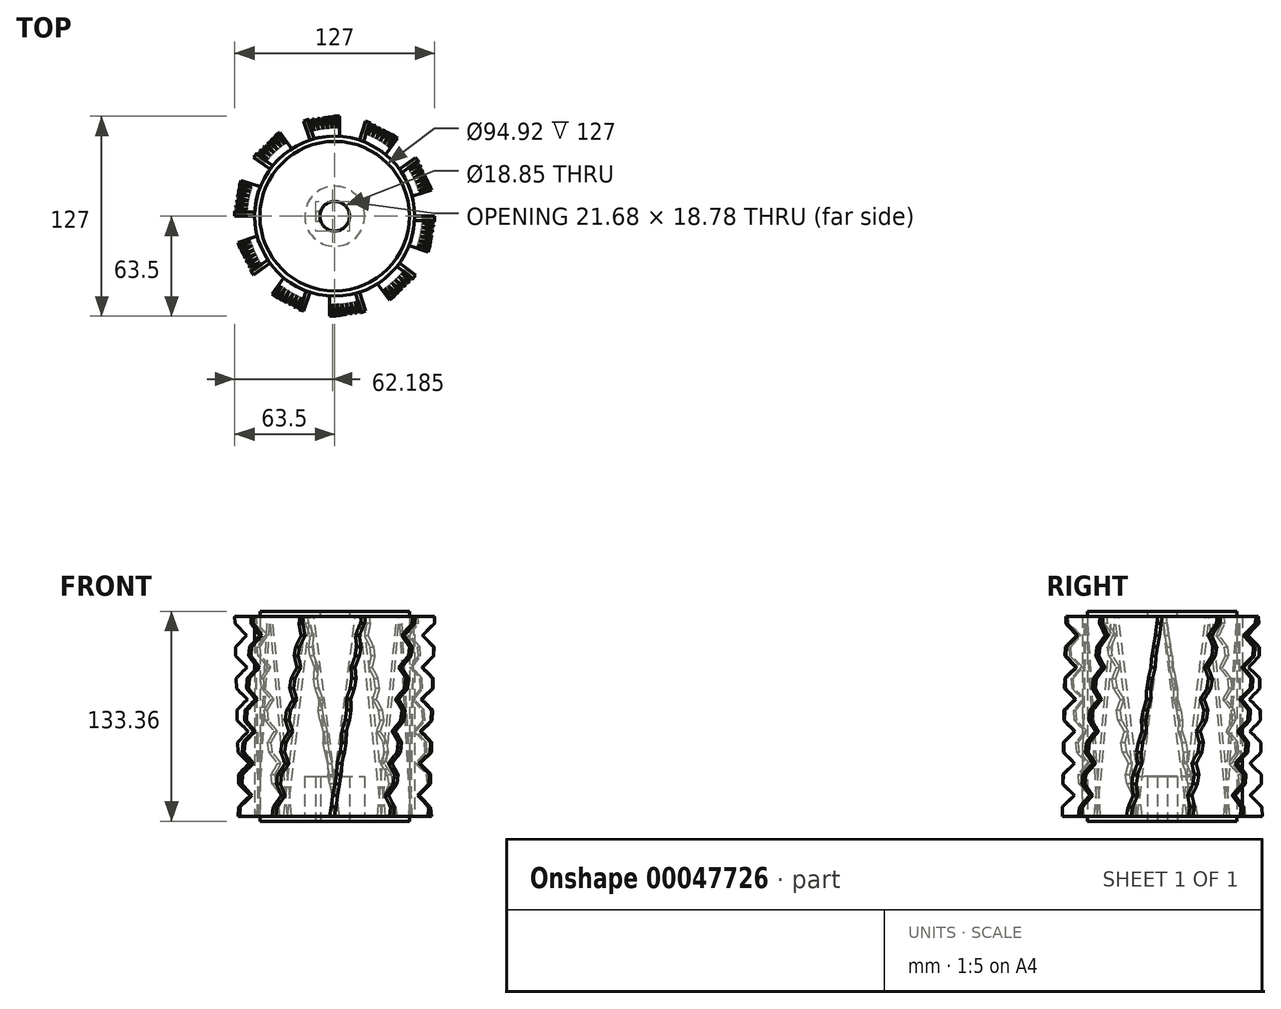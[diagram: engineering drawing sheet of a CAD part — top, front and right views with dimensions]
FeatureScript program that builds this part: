
annotation { "Feature Type Name" : "Feature", "Feature Type Description" : "" }
export const myFeature = defineFeature(function(context is Context, id is Id, definition is map)
    precondition{}
    {
        {
            var Q0;
            Q0=qCreatedBy(makeId("Top.planeOp"),FACE);
            var sketch = newSketch(context, id + "F0", { "sketchPlane" : qUnion([Q0])});
            skCircle(sketch, "E0", {"center": v(0, 0) * mm, "radius": 47.46 * mm});
            skCircle(sketch, "E1", {"center": v(0, 0) * mm, "radius": 50.8 * mm});
            skSolve(sketch);
        }
        {
            var Q0;
            Q0=makeQuery(id+"F0.imprint","IMPRINT",FACE,{"disambiguationData":[TD([[makeQuery(id+"F0.imprint","IMPRINT",EDGE,{"derivedFrom":sQuery(id+"F0.wireOp",EDGE,"E0")}),-1.0]])]});
            extrude(context, id + "F1", {"entities" : qUnion([Q0]), "endBound" : BoundingType.SYMMETRIC, "depth" : 127 * mm});
        }
        {
            var Q0;
            Q0=makeQuery(id+"F1.opExtrude","CAP_FACE",FACE,{"disambiguationData":[OSD([sQuery(id+"F0.wireOp",EDGE,"E0"),sQuery(id+"F0.wireOp",EDGE,"E1")])],"isStart":true});
            var sketch = newSketch(context, id + "F2", { "sketchPlane" : qUnion([Q0])});
            skCircle(sketch, "E2", {"center": v(0, 0) * mm, "radius": 49.21 * mm});
            skArc(sketch, "E3", {"start": v(-8.98, -3.18) * mm, "mid": v(9.53, 0) * mm, "end": v(-8.98, 3.18) * mm});
            skLineSegment(sketch, "E4.bottom", {"start": v(-12.16, -3.18) * mm, "end": v(-8.98, -3.18) * mm});
            skLineSegment(sketch, "E4.top", {"start": v(-12.16, 3.18) * mm, "end": v(-8.98, 3.18) * mm});
            skLineSegment(sketch, "E4.left", {"start": v(-12.16, -3.17) * mm, "end": v(-12.16, 3.17) * mm});
            skCircle(sketch, "E5", {"center": v(0, 0) * mm, "radius": 19.05 * mm});
            skSolve(sketch);
        }
        {
            var Q0;
            Q0=makeQuery(id+"F2.imprint","IMPRINT",FACE,{"disambiguationData":[TD([[makeQuery(id+"F2.imprint","IMPRINT",EDGE,{"derivedFrom":sQuery(id+"F2.wireOp",EDGE,"E3")}),-1.0]])]});
            extrude(context, id + "F3", {"entities" : qUnion([Q0]), "oppositeDirection" : true, "depth" : 25.4 * mm});
        }
        {
            var Q0;
            Q0=makeQuery(id+"F2.imprint","IMPRINT",FACE,{"disambiguationData":[TD([[makeQuery(id+"F2.imprint","IMPRINT",EDGE,{"derivedFrom":sQuery(id+"F2.wireOp",EDGE,"E5")}),-1.0]])]});
            var Q1;
            Q1=makeQuery(id+"F2.imprint","IMPRINT",FACE,{"disambiguationData":[TD([[makeQuery(id+"F2.imprint","IMPRINT",EDGE,{"derivedFrom":sQuery(id+"F2.wireOp",EDGE,"E3")}),-1.0]])]});
            extrude(context, id + "F4", {"entities" : qUnion([Q0, Q1]), "operationType" : NewBodyOperationType.ADD, "depth" : 3.17 * mm});
        }
        {
            var Q0;
            Q0=makeQuery(id+"F1.opExtrude","CAP_FACE",FACE,{"disambiguationData":[OSD([sQuery(id+"F0.wireOp",EDGE,"E0"),sQuery(id+"F0.wireOp",EDGE,"E1")])],"isStart":false});
            var sketch = newSketch(context, id + "F5", { "sketchPlane" : qUnion([Q0])});
            skCircle(sketch, "E6", {"center": v(0, 0) * mm, "radius": 9.43 * mm});
            skSolve(sketch);
        }
        {
            var Q0;
            Q0=makeQuery(id+"F5.imprint","IMPRINT",FACE,{"disambiguationData":[TD([[makeQuery(id+"F5.imprint","IMPRINT",EDGE,{"derivedFrom":sQuery(id+"F5.wireOp",EDGE,"E6")}),-1.0]])]});
            extrude(context, id + "F6", {"entities" : qUnion([Q0]), "depth" : 3.17 * mm});
        }
        {
            var Q0;
            Q0=makeQuery(id+"F1.opExtrude","CAP_FACE",FACE,{"disambiguationData":[OSD([sQuery(id+"F0.wireOp",EDGE,"E0"),sQuery(id+"F0.wireOp",EDGE,"E1")])],"isStart":false});
            var sketch = newSketch(context, id + "F7", { "sketchPlane" : qUnion([Q0])});
            skPoint(sketch, "E7.orphan", {"position": v(0, 0) * mm});
            skLineSegment(sketch, "E8.6.0", {"start": v(19.62, 60.4) * mm, "end": v(22.14, 59.57) * mm});
            skLineSegment(sketch, "E8.6.1", {"start": v(15.7, 48.31) * mm, "end": v(19.62, 60.4) * mm});
            skLineSegment(sketch, "E8.6.2", {"start": v(22.14, 59.57) * mm, "end": v(18.22, 47.5) * mm});
            skLineSegment(sketch, "E8.6.3", {"start": v(18.22, 47.5) * mm, "end": v(15.7, 48.31) * mm});
            skSolve(sketch);
        }
        {
            var Q0;
            Q0=makeQuery(id+"F2.imprint","IMPRINT",FACE,{"disambiguationData":[TD([[makeQuery(id+"F2.imprint","IMPRINT",EDGE,{"derivedFrom":sQuery(id+"F2.wireOp",EDGE,"E2")}),-1.0]])]});
            var sketch = newSketch(context, id + "F8", { "sketchPlane" : qUnion([Q0])});
            skLineSegment(sketch, "E9.1.0", {"start": v(39.9, -49.5) * mm, "end": v(37.32, -51.37) * mm});
            skLineSegment(sketch, "E9.1.1", {"start": v(32.43, -39.23) * mm, "end": v(29.86, -41.1) * mm});
            skLineSegment(sketch, "E9.1.2", {"start": v(39.9, -49.5) * mm, "end": v(32.43, -39.23) * mm});
            skLineSegment(sketch, "E9.1.3", {"start": v(37.32, -51.37) * mm, "end": v(29.86, -41.1) * mm});
            skSolve(sketch);
        }
        {
            var Q1;
            Q1=makeQuery(id+"F8.imprint","IMPRINT",FACE,{"disambiguationData":[TD([[makeQuery(id+"F8.imprint","IMPRINT",EDGE,{"derivedFrom":sQuery(id+"F8.wireOp",EDGE,"E9.1.0")}),-1.0]])]});
            var Q2;
            Q2=makeQuery(id+"F7.imprint","IMPRINT",FACE,{"disambiguationData":[TD([[makeQuery(id+"F7.imprint","IMPRINT",EDGE,{"derivedFrom":sQuery(id+"F7.wireOp",EDGE,"E8.6.0")}),-1.0]])]});
            loft(context, id + "F9", {"sheetProfilesArray" : [{ "sheetProfileEntities" : qUnion([Q1]) }, { "sheetProfileEntities" : qUnion([Q2]) }]});
        }
        {
            var Q0;
            Q0=makeQuery(id+"F9.opLoft","SWEPT_BODY",BODY,{"disambiguationData":[OSD([makeQuery(id+"F7.imprint","IMPRINT",FACE,{"disambiguationData":[TD([[makeQuery(id+"F7.imprint","IMPRINT",EDGE,{"derivedFrom":sQuery(id+"F7.wireOp",EDGE,"E8.6.0")}),-1.0]])]}),makeQuery(id+"F8.imprint","IMPRINT",FACE,{"disambiguationData":[TD([[makeQuery(id+"F8.imprint","IMPRINT",EDGE,{"derivedFrom":sQuery(id+"F8.wireOp",EDGE,"E9.1.0")}),-1.0]])]})])]});
            var Q1;
            Q1=makeQuery(id+"F1.opExtrude","SWEPT_FACE",FACE,{"disambiguationData":[OSD([sQuery(id+"F0.wireOp",EDGE,"E1")])]});
            circularPattern(context, id + "F10", {"entities" : qUnion([Q0]), "axis" : qUnion([Q1]), "angle" : 36 * degree, "instanceCount" : 10});
        }
        {
            var Q0;
            Q0=qCreatedBy(makeId("Right.planeOp"),FACE);
            var sketch = newSketch(context, id + "F11", { "sketchPlane" : qUnion([Q0])});
            skLineSegment(sketch, "E10.bottom", {"start": v(-64.77, 66.67) * mm, "end": v(-68.58, 66.67) * mm});
            skLineSegment(sketch, "E10.top", {"start": v(-64.77, -66.67) * mm, "end": v(-68.58, -66.67) * mm});
            skLineSegment(sketch, "E10.left", {"start": v(-55.88, -41.27) * mm, "end": v(-55.88, -50.16) * mm});
            skLineSegment(sketch, "E10.right", {"start": v(-68.58, 66.67) * mm, "end": v(-68.58, -66.67) * mm});
            skLineSegment(sketch, "E11", {"start": v(-64.77, -66.67) * mm, "end": v(-64.77, -59.06) * mm});
            skLineSegment(sketch, "E12", {"start": v(-64.77, -59.06) * mm, "end": v(-55.88, -50.16) * mm});
            skLineSegment(sketch, "E13", {"start": v(-55.88, -50.16) * mm, "end": v(-64.77, -41.27) * mm});
            skLineSegment(sketch, "E14", {"start": v(-64.77, -41.27) * mm, "end": v(-64.77, -38.73) * mm});
            skLineSegment(sketch, "E15.0.1.0", {"start": v(-64.77, -20.95) * mm, "end": v(-64.77, -18.41) * mm});
            skLineSegment(sketch, "E15.0.1.1", {"start": v(-55.88, -29.84) * mm, "end": v(-64.77, -20.95) * mm});
            skLineSegment(sketch, "E15.0.1.2", {"start": v(-64.77, -38.74) * mm, "end": v(-55.88, -29.84) * mm});
            skLineSegment(sketch, "E15.0.2.0", {"start": v(-64.77, -0.63) * mm, "end": v(-64.77, 1.9) * mm});
            skLineSegment(sketch, "E15.0.2.1", {"start": v(-55.88, -9.52) * mm, "end": v(-64.77, -0.63) * mm});
            skLineSegment(sketch, "E15.0.2.2", {"start": v(-64.77, -18.42) * mm, "end": v(-55.88, -9.52) * mm});
            skLineSegment(sketch, "E15.0.3.0", {"start": v(-64.77, 19.69) * mm, "end": v(-64.77, 22.23) * mm});
            skLineSegment(sketch, "E15.0.3.1", {"start": v(-55.88, 10.8) * mm, "end": v(-64.77, 19.69) * mm});
            skLineSegment(sketch, "E15.0.3.2", {"start": v(-64.77, 1.9) * mm, "end": v(-55.88, 10.8) * mm});
            skLineSegment(sketch, "E15.0.4.0", {"start": v(-64.77, 40) * mm, "end": v(-64.77, 42.55) * mm});
            skLineSegment(sketch, "E15.0.4.1", {"start": v(-55.88, 31.12) * mm, "end": v(-64.77, 40) * mm});
            skLineSegment(sketch, "E15.0.4.2", {"start": v(-64.77, 22.22) * mm, "end": v(-55.88, 31.11) * mm});
            skLineSegment(sketch, "E15.0.5.0", {"start": v(-64.77, 60.33) * mm, "end": v(-64.77, 62.87) * mm});
            skLineSegment(sketch, "E15.0.5.1", {"start": v(-55.88, 51.44) * mm, "end": v(-64.77, 60.33) * mm});
            skLineSegment(sketch, "E15.0.5.2", {"start": v(-64.77, 42.54) * mm, "end": v(-55.88, 51.44) * mm});
            skLineSegment(sketch, "E15.direction1", {"start": v(-64.77, -41.27) * mm, "end": v(-39.37, -41.27) * mm, "construction": true});
            skLineSegment(sketch, "E15.direction2", {"start": v(-64.77, -41.27) * mm, "end": v(-64.77, -20.95) * mm, "construction": true});
            skLineSegment(sketch, "E16", {"start": v(-64.77, 62.87) * mm, "end": v(-64.77, 66.67) * mm});
            skSolve(sketch);
        }
        {
            var Q0;
            Q0=makeQuery(id+"F11.imprint","IMPRINT",FACE,{"disambiguationData":[TD([[makeQuery(id+"F11.imprint","IMPRINT",EDGE,{"derivedFrom":sQuery(id+"F11.wireOp",EDGE,"E10.bottom")}),1.0]])]});
            var Q1;
            Q1=makeQuery(id+"F1.opExtrude","SWEPT_FACE",FACE,{"disambiguationData":[OSD([sQuery(id+"F0.wireOp",EDGE,"E1")])]});
            revolve(context, id + "F12", {"operationType" : NewBodyOperationType.REMOVE, "entities" : qUnion([Q0]), "axis" : qUnion([Q1]), "revolveType" : RevolveType.FULL, "oppositeDirection" : true});
        }
    });
